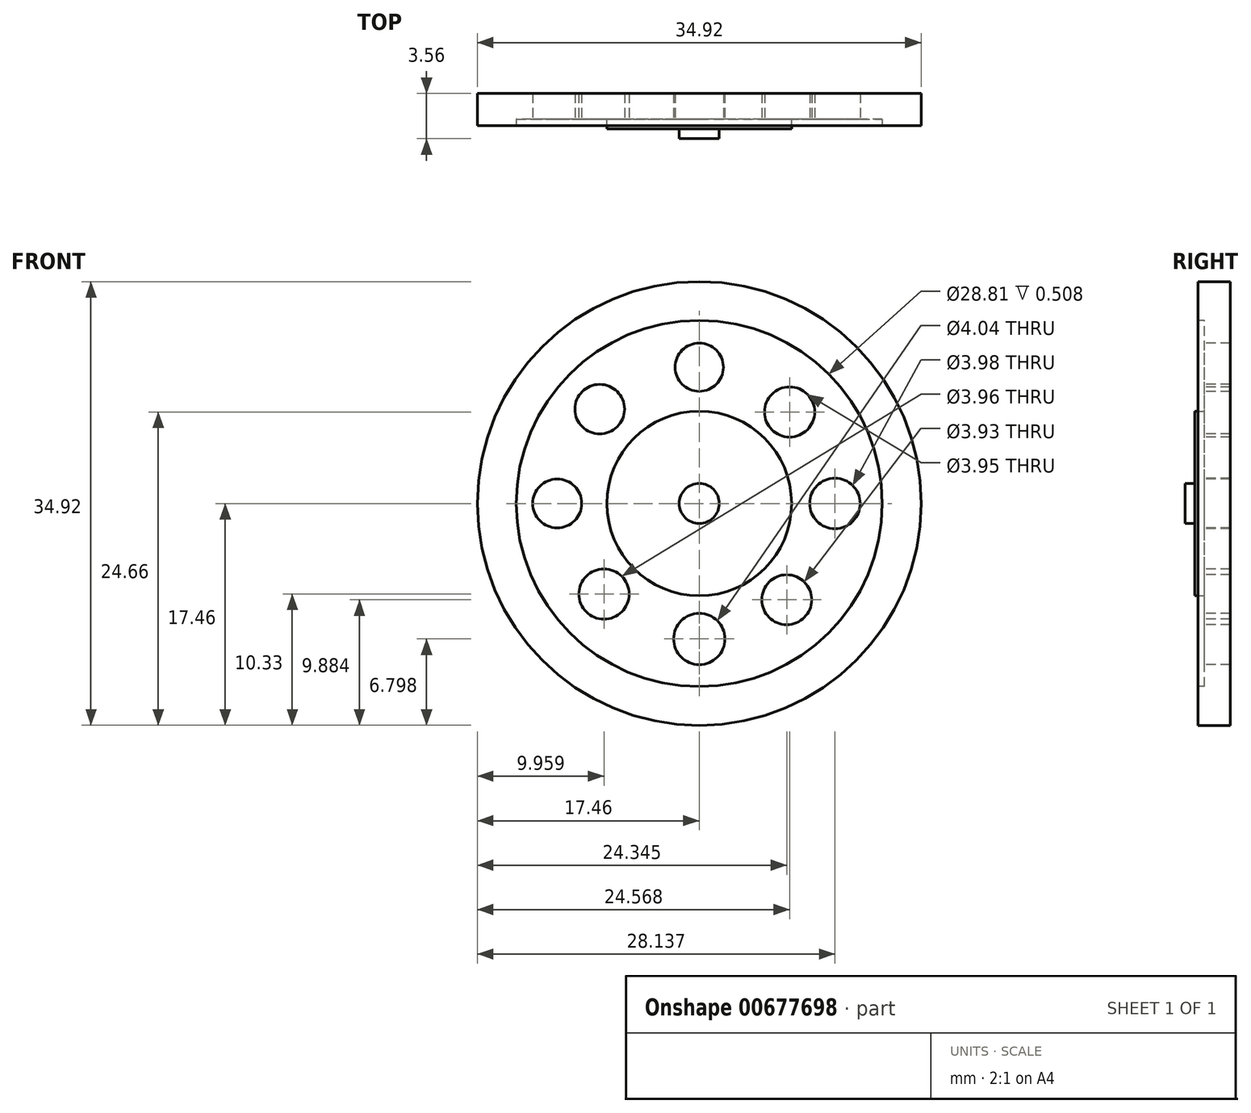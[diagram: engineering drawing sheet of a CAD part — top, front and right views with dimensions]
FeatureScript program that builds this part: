
annotation { "Feature Type Name" : "Feature", "Feature Type Description" : "" }
export const myFeature = defineFeature(function(context is Context, id is Id, definition is map)
    precondition{}
    {
        {
            var Q0;
            Q0=qCreatedBy(makeId("Front.planeOp"),FACE);
            var sketch = newSketch(context, id + "F0", { "sketchPlane" : qUnion([Q0])});
            skCircle(sketch, "E0", {"center": v(0, 0) * mm, "radius": 17.46 * mm});
            skSolve(sketch);
        }
        {
            var Q0;
            Q0=makeQuery(id+"F0.imprint","IMPRINT",FACE,{"disambiguationData":[TD([[makeQuery(id+"F0.imprint","IMPRINT",EDGE,{"derivedFrom":sQuery(id+"F0.wireOp",EDGE,"E0")}),1.0]])]});
            extrude(context, id + "F1", {"entities" : qUnion([Q0]), "depth" : 2.54 * mm, "offsetDistance" : 25.4 * mm});
        }
        {
            var Q0;
            Q0=makeQuery(id+"F1.opExtrude","CAP_FACE",FACE,{"disambiguationData":[OSD([sQuery(id+"F0.wireOp",EDGE,"E0")])],"isStart":false});
            var sketch = newSketch(context, id + "F2", { "sketchPlane" : qUnion([Q0])});
            skCircle(sketch, "E1", {"center": v(0, 0) * mm, "radius": 14.4 * mm});
            skSolve(sketch);
        }
        {
            var Q0;
            Q0=makeQuery(id+"F2.imprint","IMPRINT",FACE,{"disambiguationData":[TD([[makeQuery(id+"F2.imprint","IMPRINT",EDGE,{"derivedFrom":sQuery(id+"F2.wireOp",EDGE,"E1")}),1.0]])]});
            extrude(context, id + "F3", {"entities" : qUnion([Q0]), "operationType" : NewBodyOperationType.REMOVE, "oppositeDirection" : true, "depth" : 0.5 * mm, "offsetDistance" : 25.4 * mm});
        }
        {
            var Q0;
            Q0=makeQuery(id+"F3.boolean.opBoolean","COPY",FACE,{"derivedFrom":makeQuery(id+"F3.opExtrude","CAP_FACE",FACE,{"disambiguationData":[OSD([sQuery(id+"F2.wireOp",EDGE,"E1")])],"isStart":false})});
            var sketch = newSketch(context, id + "F4", { "sketchPlane" : qUnion([Q0])});
            skCircle(sketch, "E2", {"center": v(0, 0) * mm, "radius": 7.26 * mm});
            skSolve(sketch);
        }
        {
            var Q0;
            Q0=makeQuery(id+"F4.imprint","IMPRINT",FACE,{"disambiguationData":[TD([[makeQuery(id+"F4.imprint","IMPRINT",EDGE,{"derivedFrom":sQuery(id+"F4.wireOp",EDGE,"E2")}),1.0]])]});
            extrude(context, id + "F5", {"entities" : qUnion([Q0]), "operationType" : NewBodyOperationType.ADD, "depth" : 0.76 * mm, "offsetDistance" : 25.4 * mm});
        }
        {
            var Q0;
            Q0=makeQuery(id+"F5.opExtrude","CAP_FACE",FACE,{"disambiguationData":[OSD([sQuery(id+"F4.wireOp",EDGE,"E2")])],"isStart":false});
            var sketch = newSketch(context, id + "F6", { "sketchPlane" : qUnion([Q0])});
            skCircle(sketch, "E3", {"center": v(0, 0) * mm, "radius": 1.58 * mm});
            skSolve(sketch);
        }
        {
            var Q0;
            Q0=makeQuery(id+"F6.imprint","IMPRINT",FACE,{"disambiguationData":[TD([[makeQuery(id+"F6.imprint","IMPRINT",EDGE,{"derivedFrom":sQuery(id+"F6.wireOp",EDGE,"E3")}),1.0]])]});
            extrude(context, id + "F7", {"entities" : qUnion([Q0]), "operationType" : NewBodyOperationType.ADD, "depth" : 0.76 * mm, "offsetDistance" : 25.4 * mm});
        }
        {
            var Q0;
            Q0=makeQuery(id+"F3.boolean.opBoolean","COPY",FACE,{"derivedFrom":makeQuery(id+"F3.opExtrude","CAP_FACE",FACE,{"disambiguationData":[OSD([sQuery(id+"F2.wireOp",EDGE,"E1")])],"isStart":false})});
            var sketch = newSketch(context, id + "F8", { "sketchPlane" : qUnion([Q0])});
            skCircle(sketch, "E4", {"center": v(0, 10.72) * mm, "radius": 1.9 * mm});
            skSolve(sketch);
        }
        {
            var Q0;
            Q0=makeQuery(id+"F8.imprint","IMPRINT",FACE,{"disambiguationData":[TD([[makeQuery(id+"F8.imprint","IMPRINT",EDGE,{"derivedFrom":sQuery(id+"F8.wireOp",EDGE,"E4")}),1.0]])]});
            extrude(context, id + "F9", {"entities" : qUnion([Q0]), "operationType" : NewBodyOperationType.REMOVE, "oppositeDirection" : true, "depth" : 25.4 * mm, "offsetDistance" : 25.4 * mm});
        }
        {
            var Q0;
            Q0=makeQuery(id+"F3.boolean.opBoolean","COPY",FACE,{"derivedFrom":makeQuery(id+"F3.opExtrude","CAP_FACE",FACE,{"disambiguationData":[OSD([sQuery(id+"F2.wireOp",EDGE,"E1")])],"isStart":false})});
            var sketch = newSketch(context, id + "F10", { "sketchPlane" : qUnion([Q0])});
            skCircle(sketch, "E5", {"center": v(0, -10.66) * mm, "radius": 2.02 * mm});
            skSolve(sketch);
        }
        {
            var Q0;
            Q0=makeQuery(id+"F10.imprint","IMPRINT",FACE,{"disambiguationData":[TD([[makeQuery(id+"F10.imprint","IMPRINT",EDGE,{"derivedFrom":sQuery(id+"F10.wireOp",EDGE,"E5")}),1.0]])]});
            extrude(context, id + "F11", {"entities" : qUnion([Q0]), "operationType" : NewBodyOperationType.REMOVE, "oppositeDirection" : true, "depth" : 25.4 * mm, "offsetDistance" : 25.4 * mm});
        }
        {
            var Q0;
            Q0=makeQuery(id+"F3.boolean.opBoolean","COPY",FACE,{"derivedFrom":makeQuery(id+"F3.opExtrude","CAP_FACE",FACE,{"disambiguationData":[OSD([sQuery(id+"F2.wireOp",EDGE,"E1")])],"isStart":false})});
            var sketch = newSketch(context, id + "F12", { "sketchPlane" : qUnion([Q0])});
            skCircle(sketch, "E6", {"center": v(-11.18, 0) * mm, "radius": 1.93 * mm});
            skSolve(sketch);
        }
        {
            var Q0;
            Q0=makeQuery(id+"F12.imprint","IMPRINT",FACE,{"disambiguationData":[TD([[makeQuery(id+"F12.imprint","IMPRINT",EDGE,{"derivedFrom":sQuery(id+"F12.wireOp",EDGE,"E6")}),1.0]])]});
            extrude(context, id + "F13", {"entities" : qUnion([Q0]), "operationType" : NewBodyOperationType.REMOVE, "oppositeDirection" : true, "depth" : 25.4 * mm, "offsetDistance" : 25.4 * mm});
        }
        {
            var Q0;
            Q0=makeQuery(id+"F3.boolean.opBoolean","COPY",FACE,{"derivedFrom":makeQuery(id+"F3.opExtrude","CAP_FACE",FACE,{"disambiguationData":[OSD([sQuery(id+"F2.wireOp",EDGE,"E1")])],"isStart":false})});
            var sketch = newSketch(context, id + "F14", { "sketchPlane" : qUnion([Q0])});
            skCircle(sketch, "E7", {"center": v(10.68, 0) * mm, "radius": 1.99 * mm});
            skSolve(sketch);
        }
        {
            var Q0;
            Q0=makeQuery(id+"F14.imprint","IMPRINT",FACE,{"disambiguationData":[TD([[makeQuery(id+"F14.imprint","IMPRINT",EDGE,{"derivedFrom":sQuery(id+"F14.wireOp",EDGE,"E7")}),1.0]])]});
            extrude(context, id + "F15", {"entities" : qUnion([Q0]), "operationType" : NewBodyOperationType.REMOVE, "oppositeDirection" : true, "depth" : 25.4 * mm, "offsetDistance" : 25.4 * mm});
        }
        {
            var Q0;
            Q0=makeQuery(id+"F3.boolean.opBoolean","COPY",FACE,{"derivedFrom":makeQuery(id+"F3.opExtrude","CAP_FACE",FACE,{"disambiguationData":[OSD([sQuery(id+"F2.wireOp",EDGE,"E1")])],"isStart":false})});
            var sketch = newSketch(context, id + "F16", { "sketchPlane" : qUnion([Q0])});
            skCircle(sketch, "E8", {"center": v(-7.84, 7.42) * mm, "radius": 1.95 * mm});
            skSolve(sketch);
        }
        {
            var Q0;
            Q0=makeQuery(id+"F16.imprint","IMPRINT",FACE,{"disambiguationData":[TD([[makeQuery(id+"F16.imprint","IMPRINT",EDGE,{"derivedFrom":sQuery(id+"F16.wireOp",EDGE,"E8")}),1.0]])]});
            extrude(context, id + "F17", {"entities" : qUnion([Q0]), "operationType" : NewBodyOperationType.REMOVE, "oppositeDirection" : true, "depth" : 25.4 * mm, "offsetDistance" : 25.4 * mm});
        }
        {
            var Q0;
            Q0=makeQuery(id+"F3.boolean.opBoolean","COPY",FACE,{"derivedFrom":makeQuery(id+"F3.opExtrude","CAP_FACE",FACE,{"disambiguationData":[OSD([sQuery(id+"F2.wireOp",EDGE,"E1")])],"isStart":false})});
            var sketch = newSketch(context, id + "F18", { "sketchPlane" : qUnion([Q0])});
            skCircle(sketch, "E9", {"center": v(-7.5, -7.13) * mm, "radius": 1.98 * mm});
            skSolve(sketch);
        }
        {
            var Q0;
            Q0=makeQuery(id+"F18.imprint","IMPRINT",FACE,{"disambiguationData":[TD([[makeQuery(id+"F18.imprint","IMPRINT",EDGE,{"derivedFrom":sQuery(id+"F18.wireOp",EDGE,"E9")}),1.0]])]});
            extrude(context, id + "F19", {"entities" : qUnion([Q0]), "operationType" : NewBodyOperationType.REMOVE, "oppositeDirection" : true, "depth" : 25.4 * mm, "offsetDistance" : 25.4 * mm});
        }
        {
            var Q0;
            Q0=makeQuery(id+"F3.boolean.opBoolean","COPY",FACE,{"derivedFrom":makeQuery(id+"F3.opExtrude","CAP_FACE",FACE,{"disambiguationData":[OSD([sQuery(id+"F2.wireOp",EDGE,"E1")])],"isStart":false})});
            var sketch = newSketch(context, id + "F20", { "sketchPlane" : qUnion([Q0])});
            skCircle(sketch, "E10", {"center": v(6.89, -7.58) * mm, "radius": 1.96 * mm});
            skSolve(sketch);
        }
        {
            var Q0;
            Q0=makeQuery(id+"F20.imprint","IMPRINT",FACE,{"disambiguationData":[TD([[makeQuery(id+"F20.imprint","IMPRINT",EDGE,{"derivedFrom":sQuery(id+"F20.wireOp",EDGE,"E10")}),1.0]])]});
            extrude(context, id + "F21", {"entities" : qUnion([Q0]), "operationType" : NewBodyOperationType.REMOVE, "oppositeDirection" : true, "depth" : 25.4 * mm, "offsetDistance" : 25.4 * mm});
        }
        {
            var Q0;
            Q0=makeQuery(id+"F3.boolean.opBoolean","COPY",FACE,{"derivedFrom":makeQuery(id+"F3.opExtrude","CAP_FACE",FACE,{"disambiguationData":[OSD([sQuery(id+"F2.wireOp",EDGE,"E1")])],"isStart":false})});
            var sketch = newSketch(context, id + "F22", { "sketchPlane" : qUnion([Q0])});
            skCircle(sketch, "E11", {"center": v(7.1, 7.2) * mm, "radius": 1.97 * mm});
            skSolve(sketch);
        }
        {
            var Q0;
            Q0=makeQuery(id+"F22.imprint","IMPRINT",FACE,{"disambiguationData":[TD([[makeQuery(id+"F22.imprint","IMPRINT",EDGE,{"derivedFrom":sQuery(id+"F22.wireOp",EDGE,"E11")}),1.0]])]});
            extrude(context, id + "F23", {"entities" : qUnion([Q0]), "operationType" : NewBodyOperationType.REMOVE, "oppositeDirection" : true, "depth" : 25.4 * mm, "offsetDistance" : 25.4 * mm});
        }
        {
            var Q0;
            Q0=makeQuery(id+"F1.opExtrude","CAP_FACE",FACE,{"disambiguationData":[OSD([sQuery(id+"F0.wireOp",EDGE,"E0")])],"isStart":true});
            var sketch = newSketch(context, id + "F24", { "sketchPlane" : qUnion([Q0])});
            skCircle(sketch, "E12", {"center": v(0, 0) * mm, "radius": 0.96 * mm});
            skSolve(sketch);
        }
        {
            var Q0;
            Q0=sQuery(id+"F24.wireOp",EDGE,"E12");
            extrude(context, id + "F25", {"bodyType" : ToolBodyType.SURFACE, "surfaceEntities" : qUnion([Q0]), "depth" : 12.7 * mm, "offsetDistance" : 25.4 * mm});
        }
    });
